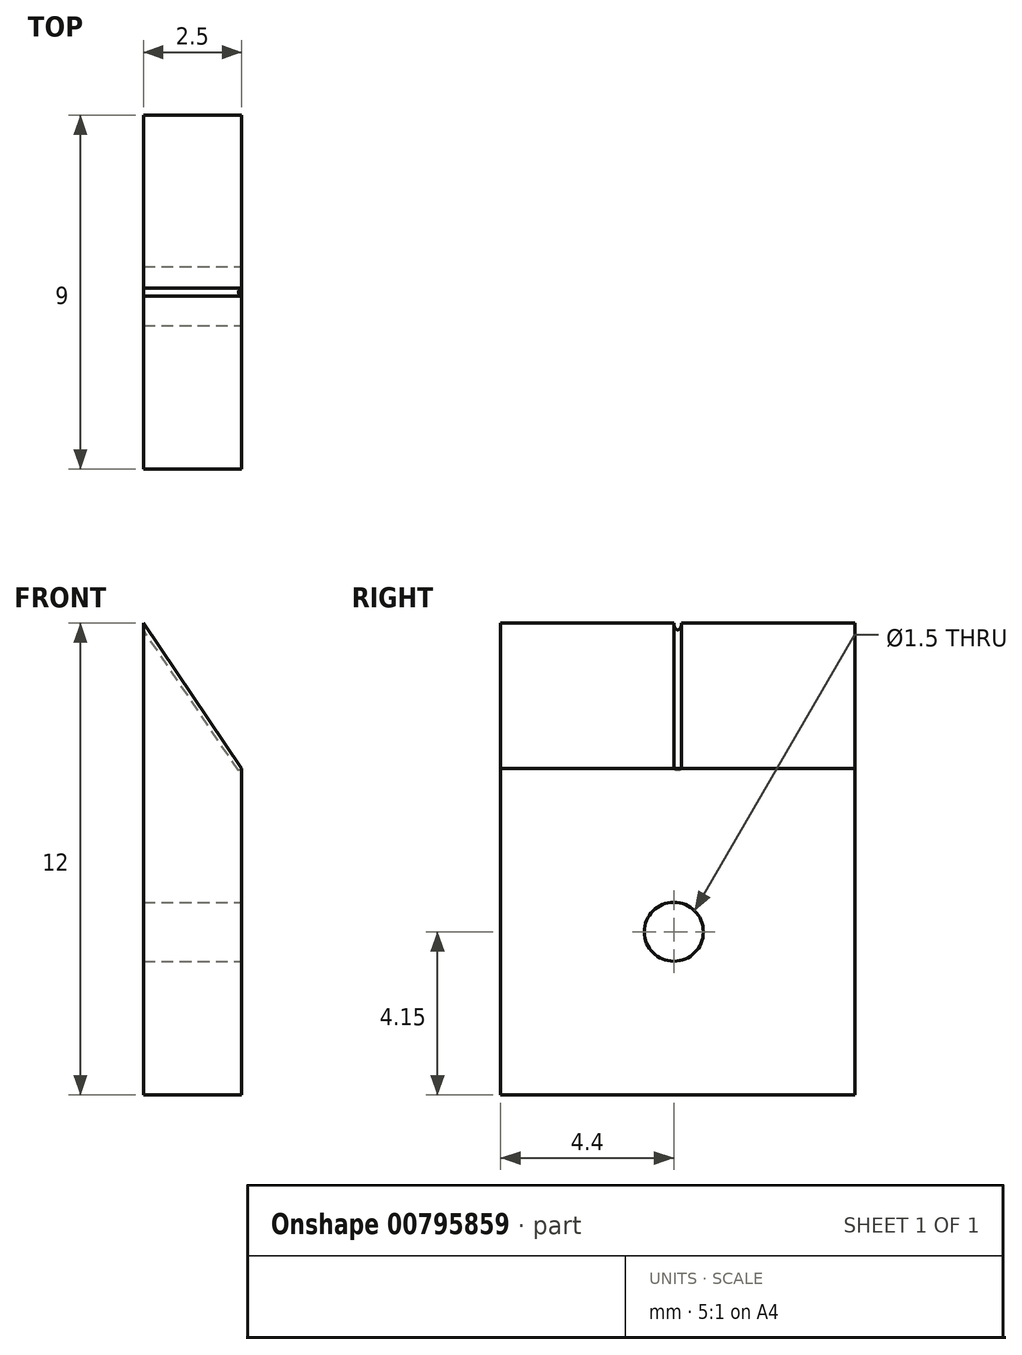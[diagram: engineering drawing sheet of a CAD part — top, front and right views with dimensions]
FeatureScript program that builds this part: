
annotation { "Feature Type Name" : "Feature", "Feature Type Description" : "" }
export const myFeature = defineFeature(function(context is Context, id is Id, definition is map)
    precondition{}
    {
        {
            var Q0;
            Q0=qCreatedBy(makeId("Front.planeOp"),FACE);
            var sketch = newSketch(context, id + "F0", { "sketchPlane" : qUnion([Q0])});
            skLineSegment(sketch, "E0", {"start": v(-1.25, 0) * mm, "end": v(1.25, 0) * mm});
            skLineSegment(sketch, "E1", {"start": v(1.25, 0) * mm, "end": v(1.25, 8.3) * mm});
            skLineSegment(sketch, "E2", {"start": v(1.25, 8.3) * mm, "end": v(-1.25, 12) * mm});
            skLineSegment(sketch, "E3", {"start": v(-1.25, 12) * mm, "end": v(-1.25, 0) * mm});
            skSolve(sketch);
        }
        {
            var Q0;
            Q0 = qSketchRegion(id + "F0", true);
            extrude(context, id + "F1", {"entities" : qUnion([Q0]), "depth" : 9 * mm, "offsetDistance" : 25 * mm});
        }
        {
            var Q0;
            Q0=makeQuery(id+"F1.opExtrude","SWEPT_FACE",FACE,{"disambiguationData":[OSD([sQuery(id+"F0.wireOp",EDGE,"E2")])]});
            var sketch = newSketch(context, id + "F2", { "sketchPlane" : qUnion([Q0])});
            skLineSegment(sketch, "E4", {"start": v(-4.5, 10.64) * mm, "end": v(-4.5, 6.18) * mm});
            skLineSegment(sketch, "E5", {"start": v(-4.5, 6.18) * mm, "end": v(-4.6, 6.18) * mm});
            skLineSegment(sketch, "E6", {"start": v(-4.6, 6.18) * mm, "end": v(-4.6, 10.64) * mm});
            skLineSegment(sketch, "E7", {"start": v(-4.6, 10.64) * mm, "end": v(-4.5, 10.64) * mm});
            skSolve(sketch);
        }
        {
            var Q0;
            Q0 = qSketchRegion(id + "F2", true);
            var Q1;
            Q1=sQuery(id+"F2.wireOp",EDGE,"E4");
            revolve(context, id + "F3", {"operationType" : NewBodyOperationType.REMOVE, "surfaceOperationType" : NewSurfaceOperationType.NEW, "entities" : qUnion([Q0]), "axis" : qUnion([Q1]), "revolveType" : RevolveType.FULL});
        }
        {
            var Q0;
            Q0=makeQuery(id+"F1.opExtrude","SWEPT_FACE",FACE,{"disambiguationData":[OSD([sQuery(id+"F0.wireOp",EDGE,"E1")])]});
            var sketch = newSketch(context, id + "F4", { "sketchPlane" : qUnion([Q0])});
            skCircle(sketch, "E8", {"center": v(-4.6, 4.15) * mm, "radius": 0.75 * mm});
            skLineSegment(sketch, "E9", {"start": v(-4.6, 8.3) * mm, "end": v(-4.6, 0) * mm, "construction": true});
            skLineSegment(sketch, "E10", {"start": v(-9, 4.15) * mm, "end": v(0, 4.15) * mm, "construction": true});
            skSolve(sketch);
        }
        {
            var Q0;
            Q0 = qSketchRegion(id + "F4", true);
            extrude(context, id + "F5", {"entities" : qUnion([Q0]), "operationType" : NewBodyOperationType.REMOVE, "endBound" : BoundingType.THROUGH_ALL, "oppositeDirection" : true, "depth" : 25 * mm, "offsetDistance" : 25 * mm});
        }
    });
